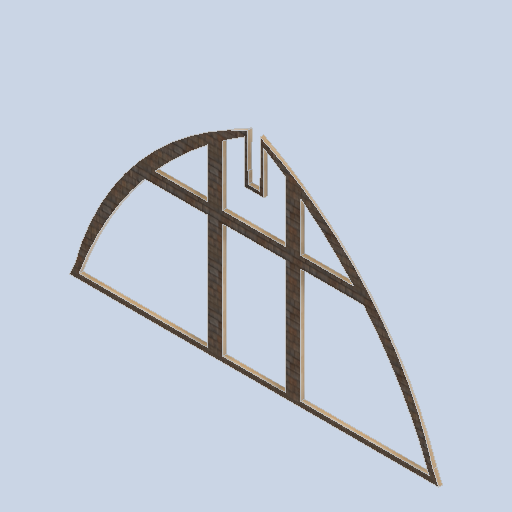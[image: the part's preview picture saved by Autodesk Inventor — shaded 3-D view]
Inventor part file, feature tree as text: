
AUTODESK INVENTOR PART (.ipt)
format: ipt  version: 2024.2 (Build 282272000, 272)  size: 240,128 bytes
history: native  units: in
note: dims shown in document units (in); Inventor stores cm internally (conversion verified against a paired STEP export)
features: other x3, sketch x3, plane x2
ambient origin geometry x8: Origin, YZ Plane, XZ Plane, XY Plane, X Axis, Y Axis, Z Axis, Center Point
bodies: Solid1 (feature_tree)
feature tree (8):
  other  "curve_front_wall_frame.ipt"
  other  "Solid1::curve_front_wall_frame.ipt"
  other  "TaggingFeature1"
  sketch  "Sketch1"  dims[d0=0.3937in]
  sketch  "Sketch4"
  sketch  "Sketch5"
  plane  "Work Plane1"
  plane  "Work Plane2"
